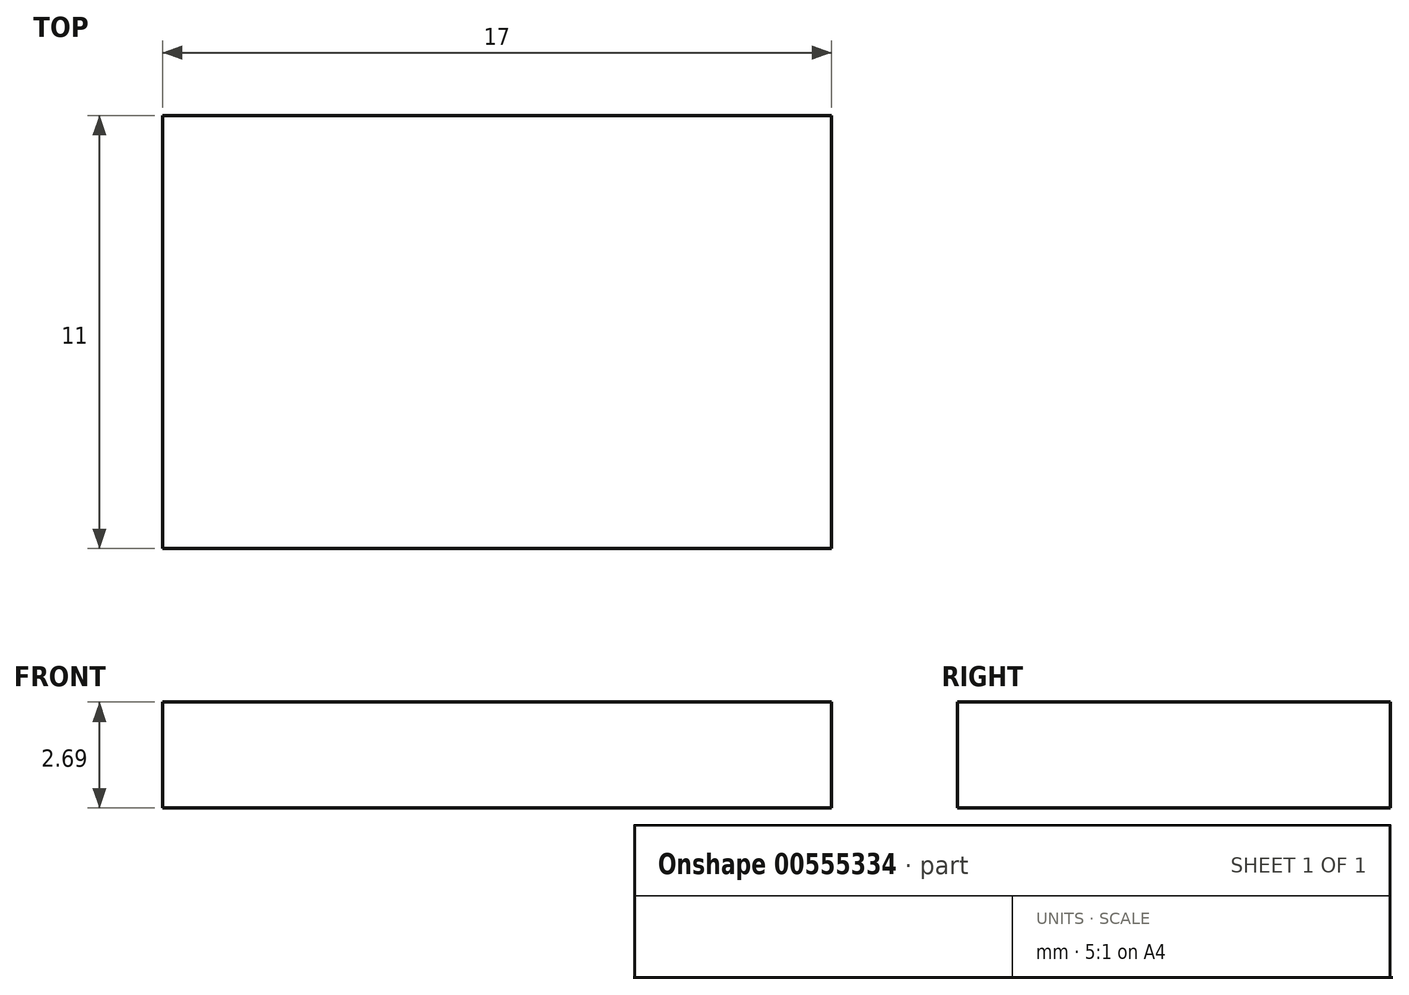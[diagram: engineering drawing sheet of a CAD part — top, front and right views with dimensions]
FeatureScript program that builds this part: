
annotation { "Feature Type Name" : "Feature", "Feature Type Description" : "" }
export const myFeature = defineFeature(function(context is Context, id is Id, definition is map)
    precondition{}
    {
        {
            var Q0;
            Q0=qCreatedBy(makeId("Top.planeOp"),FACE);
            var sketch = newSketch(context, id + "F0", { "sketchPlane" : qUnion([Q0])});
            skLineSegment(sketch, "E0.bottom", {"start": v(-8.5, 5.5) * mm, "end": v(8.5, 5.5) * mm});
            skLineSegment(sketch, "E0.top", {"start": v(-8.5, -5.5) * mm, "end": v(8.5, -5.5) * mm});
            skLineSegment(sketch, "E0.left", {"start": v(-8.5, 5.5) * mm, "end": v(-8.5, -5.5) * mm});
            skLineSegment(sketch, "E0.right", {"start": v(8.5, 5.5) * mm, "end": v(8.5, -5.5) * mm});
            skPoint(sketch, "E0.middle", {"position": v(0, 0) * mm});
            skSolve(sketch);
        }
        {
            var Q0;
            Q0 = qSketchRegion(id + "F0", true);
            extrude(context, id + "F1", {"entities" : qUnion([Q0]), "depth" : 2.69 * mm, "offsetDistance" : 25.4 * mm});
        }
    });
